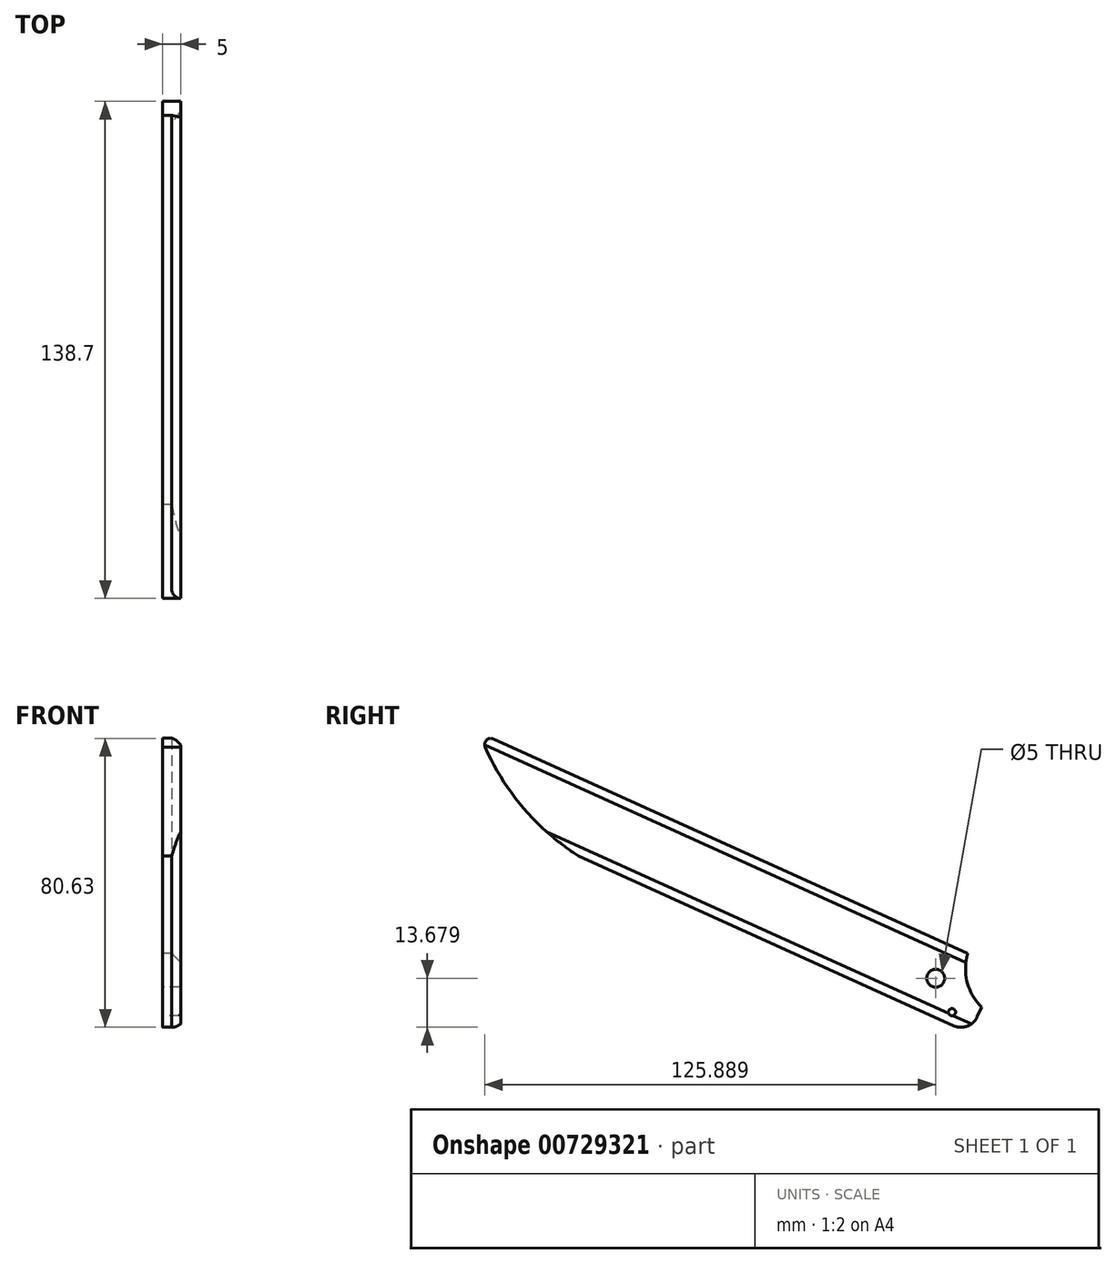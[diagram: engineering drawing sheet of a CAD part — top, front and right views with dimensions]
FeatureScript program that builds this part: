
annotation { "Feature Type Name" : "Feature", "Feature Type Description" : "" }
export const myFeature = defineFeature(function(context is Context, id is Id, definition is map)
    precondition{}
    {
        {
            var Q0;
            Q0=qCreatedBy(makeId("Right.planeOp"),FACE);
            var sketch = newSketch(context, id + "F0", { "sketchPlane" : qUnion([Q0])});
            skLineSegment(sketch, "E0", {"start": v(-133.72, 3.82) * mm, "end": v(-238.35, 51.14) * mm});
            skLineSegment(sketch, "E1", {"start": v(-262.15, 83.85) * mm, "end": v(-129.77, 23.98) * mm});
            skLineSegment(sketch, "E2", {"start": v(-125.9, 8.98) * mm, "end": v(-127.1, 6.31) * mm});
            skCircle(sketch, "E3", {"center": v(-138.71, 17.05) * mm, "radius": 2.5 * mm});
            skCircle(sketch, "E4.0", {"center": v(-138.71, 17.05) * mm, "radius": 10.5 * mm, "construction": true});
            skLineSegment(sketch, "E5.0", {"start": v(-141.05, 12.77) * mm, "end": v(-129.77, 7.66) * mm, "construction": true});
            skCircle(sketch, "E6", {"center": v(-132.24, 8.78) * mm, "radius": 1 * mm, "construction": true});
            skPoint(sketch, "E7.visualSharp", {"position": v(-129.16, 1.76) * mm});
            skArc(sketch, "E7.filletArc", {"start": v(-133.72, 3.82) * mm, "mid": v(-129.9, 3.7) * mm, "end": v(-127.1, 6.31) * mm});
            skPoint(sketch, "E8.visualSharp", {"position": v(-120.92, 19.98) * mm});
            skArc(sketch, "E9", {"start": v(-264.5, 81.67) * mm, "mid": v(-253.7, 64.46) * mm, "end": v(-238.35, 51.14) * mm});
            skPoint(sketch, "E10.start.orphan", {"position": v(-256.73, 59.45) * mm});
            skLineSegment(sketch, "E11", {"start": v(-262.15, 83.85) * mm, "end": v(-224.51, 66.83) * mm});
            skArc(sketch, "E12", {"start": v(-262.15, 83.85) * mm, "mid": v(-264.13, 83.46) * mm, "end": v(-264.4, 81.47) * mm});
            skLineSegment(sketch, "E13", {"start": v(-138.71, 17.05) * mm, "end": v(-142.83, 7.94) * mm, "construction": true});
            skCircle(sketch, "E14", {"center": v(-138.71, 17.05) * mm, "radius": 117.85 * mm, "construction": true});
            skLineSegment(sketch, "E15", {"start": v(-273.63, 72.67) * mm, "end": v(-218.97, 47.95) * mm, "construction": true});
            skCircle(sketch, "E16", {"center": v(-248.03, 61.09) * mm, "radius": 1 * mm, "construction": true});
            skArc(sketch, "E17", {"start": v(-129.77, 23.98) * mm, "mid": v(-129.92, 15.94) * mm, "end": v(-125.9, 8.98) * mm});
            skLineSegment(sketch, "E18", {"start": v(-138.71, 17.05) * mm, "end": v(-131.38, 13.73) * mm, "construction": true});
            skLineSegment(sketch, "E19", {"start": v(-131.38, 13.73) * mm, "end": v(-134.16, 7.59) * mm, "construction": true});
            skCircle(sketch, "E20", {"center": v(-134.16, 7.59) * mm, "radius": 1 * mm});
            skSolve(sketch);
        }
        {
            var Q0;
            Q0 = qSketchRegion(id + "F0", true);
            extrude(context, id + "F1", {"entities" : qUnion([Q0]), "depth" : 5 * mm, "offsetDistance" : 25 * mm});
        }
        {
            var Q0;
            Q0=makeQuery(id+"F1.opExtrude","CAP_EDGE",EDGE,{"disambiguationData":[OSD([sQuery(id+"F0.wireOp",EDGE,"E0")])],"isStart":false});
            var Q1;
            Q1=makeQuery(id+"F1.opExtrude","CAP_EDGE",EDGE,{"disambiguationData":[OSD([sQuery(id+"F0.wireOp",EDGE,"E1"),sQuery(id+"F0.wireOp",EDGE,"E11")])],"isStart":false});
            chamfer(context, id + "F2", {"entities" : qUnion([Q0, Q1]), "width" : 2.5 * mm});
        }
    });
